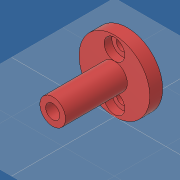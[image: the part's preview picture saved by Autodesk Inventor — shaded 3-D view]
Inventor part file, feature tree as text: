
AUTODESK INVENTOR PART (.ipt)
format: ipt  version: 2019 (Build 230136000, 136)  size: 117,760 bytes
history: native  units: mm
features: extrude x4, sketch x1
ambient origin geometry x8: Origin, YZ Plane, XZ Plane, XY Plane, X Axis, Y Axis, Z Axis, Center Point
bodies: Volumenkörper1 (feature_tree)
feature tree (5):
  sketch  "Skizze1"  dims[d0=27.5mm d1=10.0mm d4=8.0mm d5=18.0mm d6=4.5mm d7=5.5mm d8=5.0mm d9=0.0mm d10=3.0mm d11=0.0mm d12=24.0mm d13=0.0mm d14=7.0mm d15=24.0mm d16=0.0mm]
  extrude  "Extrusion1"  Depth=24.0mm
  extrude  "Extrusion2"  Depth=5.0mm TaperAngle=0.0deg
  extrude  "Extrusion3"  Depth=3.0mm TaperAngle=0.0deg
  extrude  "Extrusion4"  Depth=24.0mm TaperAngle=0.0deg
